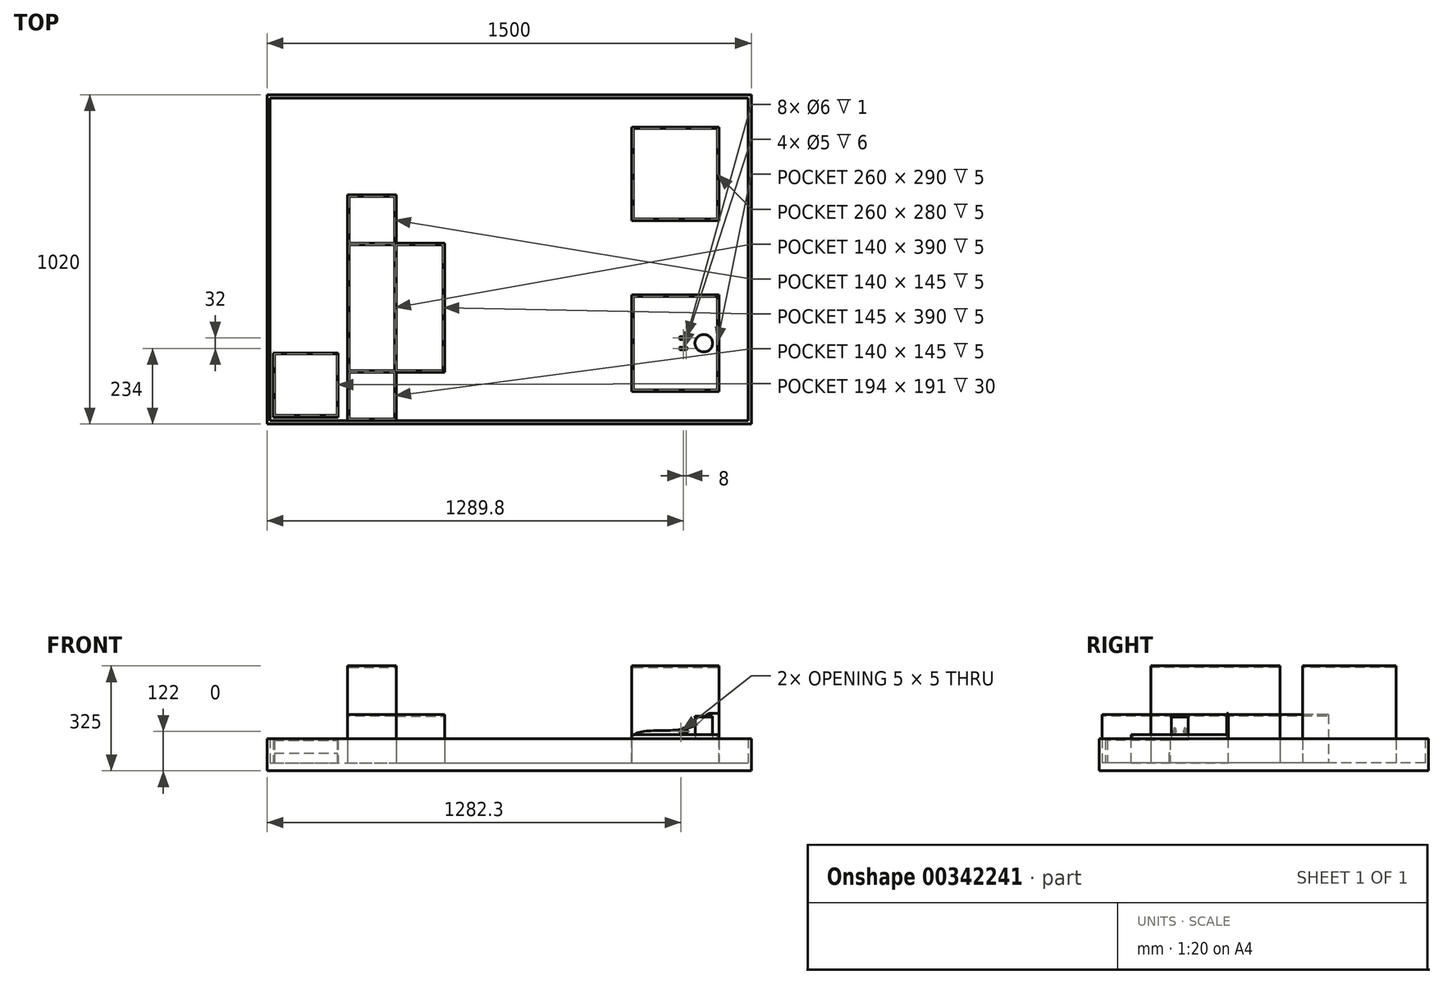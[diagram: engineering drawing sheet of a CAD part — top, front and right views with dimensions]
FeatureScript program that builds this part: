
annotation { "Feature Type Name" : "Feature", "Feature Type Description" : "" }
export const myFeature = defineFeature(function(context is Context, id is Id, definition is map)
    precondition{}
    {
        {
            var Q0;
            Q0=qCreatedBy(makeId("Top.planeOp"),FACE);
            var sketch = newSketch(context, id + "F0", { "sketchPlane" : qUnion([Q0])});
            skCircle(sketch, "E0", {"center": v(0, 0) * mm, "radius": 27.2 * mm});
            skSolve(sketch);
        }
        {
            var Q0;
            Q0=qSketchRegion(id+"F0",true);
            extrude(context, id + "F1", {"entities" : qUnion([Q0]), "depth" : 2.83 * mm});
        }
        {
            var Q0;
            Q0=makeQuery(id+"F1.opExtrude","CAP_FACE",FACE,{"disambiguationData":[OSD([sQuery(id+"F0.wireOp",EDGE,"E0")])],"isStart":false});
            var sketch = newSketch(context, id + "F2", { "sketchPlane" : qUnion([Q0])});
            skCircle(sketch, "E1", {"center": v(0, 0) * mm, "radius": 26.4 * mm});
            skSolve(sketch);
        }
        {
            var Q0;
            Q0=qSketchRegion(id+"F2",true);
            extrude(context, id + "F3", {"entities" : qUnion([Q0]), "operationType" : NewBodyOperationType.ADD, "depth" : 67.36 * mm});
        }
        {
            var Q0;
            Q0=makeQuery(id+"F3.opExtrude","CAP_FACE",FACE,{"disambiguationData":[OSD([sQuery(id+"F2.wireOp",EDGE,"E1")])],"isStart":false});
            var sketch = newSketch(context, id + "F4", { "sketchPlane" : qUnion([Q0])});
            skCircle(sketch, "E2", {"center": v(0, 0) * mm, "radius": 27.2 * mm});
            skSolve(sketch);
        }
        {
            var Q0;
            Q0=qSketchRegion(id+"F4",true);
            extrude(context, id + "F5", {"entities" : qUnion([Q0]), "operationType" : NewBodyOperationType.ADD, "depth" : 2.83 * mm});
        }
        {
            var Q0;
            Q0=makeQuery(id+"F5.opExtrude","CAP_FACE",FACE,{"disambiguationData":[OSD([sQuery(id+"F4.wireOp",EDGE,"E2")])],"isStart":false});
            var sketch = newSketch(context, id + "F6", { "sketchPlane" : qUnion([Q0])});
            skSolve(sketch);
        }
        {
            var Q0;
            Q0=qCreatedBy(makeId("Top.planeOp"),FACE);
            cPlane(context, id + "F7", {"entities" : qUnion([Q0]), "cplaneType" : CPlaneType.OFFSET, "offset" : 25 * mm, "width" : 150 * mm, "height" : 150 * mm});
        }
        {
            var Q0;
            Q0=makeQuery(id+"F6.imprint","IMPRINT",FACE,{"disambiguationData":[TD([[makeQuery(id+"F6.imprint","IMPRINT",EDGE,{"derivedFrom":makeQuery(id+"F5.opExtrude","CAP_EDGE",EDGE,{"disambiguationData":[OSD([sQuery(id+"F4.wireOp",EDGE,"E2")])],"isStart":false})}),1.0]])]});
            var sketch = newSketch(context, id + "F8", { "sketchPlane" : qUnion([Q0])});
            skSolve(sketch);
        }
        {
            var Q0;
            Q0=qCreatedBy(makeId("Top.planeOp"),FACE);
            var sketch = newSketch(context, id + "F9", { "sketchPlane" : qUnion([Q0])});
            skLineSegment(sketch, "E3.bottom", {"start": v(-222.8, -150) * mm, "end": v(47.2, -150) * mm});
            skLineSegment(sketch, "E3.top", {"start": v(-222.8, 150) * mm, "end": v(47.2, 150) * mm});
            skLineSegment(sketch, "E3.left", {"start": v(-222.8, -150) * mm, "end": v(-222.8, 150) * mm});
            skLineSegment(sketch, "E3.right", {"start": v(47.2, -150) * mm, "end": v(47.2, 150) * mm});
            skSolve(sketch);
        }
        {
            var Q0;
            Q0=qSketchRegion(id+"F9",true);
            extrude(context, id + "F10", {"entities" : qUnion([Q0]), "oppositeDirection" : true, "depth" : 72 * mm});
        }
        {
            var Q0;
            Q0=makeQuery(id+"F10.opExtrude","CAP_FACE",FACE,{"disambiguationData":[OSD([sQuery(id+"F9.wireOp",EDGE,"E3.bottom"),sQuery(id+"F9.wireOp",EDGE,"E3.top"),sQuery(id+"F9.wireOp",EDGE,"E3.left"),sQuery(id+"F9.wireOp",EDGE,"E3.right")])],"isStart":true});
            var sketch = newSketch(context, id + "F11", { "sketchPlane" : qUnion([Q0])});
            skLineSegment(sketch, "E4.bottom", {"start": v(-222.8, -150) * mm, "end": v(47.2, -150) * mm});
            skLineSegment(sketch, "E4.top", {"start": v(-222.8, -145) * mm, "end": v(42.2, -145) * mm});
            skLineSegment(sketch, "E4.left", {"start": v(-222.8, -150) * mm, "end": v(-222.8, -145) * mm});
            skLineSegment(sketch, "E5.bottom", {"start": v(47.2, 150) * mm, "end": v(42.2, 150) * mm});
            skLineSegment(sketch, "E5.left", {"start": v(47.2, 150) * mm, "end": v(47.2, -150) * mm});
            skLineSegment(sketch, "E5.right", {"start": v(42.2, 150) * mm, "end": v(42.2, -145) * mm});
            skSolve(sketch);
        }
        {
            var Q0;
            Q0=qSketchRegion(id+"F11",true);
            extrude(context, id + "F12", {"entities" : qUnion([Q0]), "operationType" : NewBodyOperationType.ADD, "depth" : 15 * mm});
        }
        {
            var Q0;
            Q0=makeQuery(id+"F12.boolean.opBoolean","MERGE",FACE,{"derivedFrom":[makeQuery(id+"F10.opExtrude","SWEPT_FACE",FACE,{"disambiguationData":[OSD([sQuery(id+"F9.wireOp",EDGE,"E3.top")])]}),makeQuery(id+"F12.opExtrude","SWEPT_FACE",FACE,{"disambiguationData":[OSD([sQuery(id+"F11.wireOp",EDGE,"E5.bottom")])]})]});
            var sketch = newSketch(context, id + "F13", { "sketchPlane" : qUnion([Q0])});
            skLineSegment(sketch, "E6", {"start": v(-47.2, 81.36) * mm, "end": v(-21.31, 81.36) * mm});
            skFitSpline(sketch, "E7", {"points": [v(-21.31, 81.36) * mm, v(15.24, 52.01) * mm, v(114.14, 28.17) * mm, v(222.8, 0) * mm], "startDerivative": vector(181.02, 0.3) * mm, "endDerivative": vector(-1.73, -239.85) * mm});
            skLineSegment(sketch, "E8", {"start": v(-47.2, 81.36) * mm, "end": v(-47.2, -72) * mm});
            skLineSegment(sketch, "E9", {"start": v(-47.2, -72) * mm, "end": v(222.8, -72) * mm});
            skLineSegment(sketch, "E10", {"start": v(222.8, -72) * mm, "end": v(222.8, 0) * mm});
            skSolve(sketch);
        }
        {
            var Q0;
            Q0=qSketchRegion(id+"F13",true);
            extrude(context, id + "F14", {"entities" : qUnion([Q0]), "operationType" : NewBodyOperationType.ADD, "oppositeDirection" : true, "depth" : 5 * mm});
        }
        {
            var Q0;
            Q0=makeQuery(id+"F10.opExtrude","CAP_FACE",FACE,{"disambiguationData":[OSD([sQuery(id+"F9.wireOp",EDGE,"E3.bottom"),sQuery(id+"F9.wireOp",EDGE,"E3.top"),sQuery(id+"F9.wireOp",EDGE,"E3.left"),sQuery(id+"F9.wireOp",EDGE,"E3.right")])],"isStart":true});
            var sketch = newSketch(context, id + "F15", { "sketchPlane" : qUnion([Q0])});
            skLineSegment(sketch, "E11.bottom", {"start": v(-222.8, 145) * mm, "end": v(-217.8, 145) * mm});
            skLineSegment(sketch, "E11.top", {"start": v(-222.8, -145) * mm, "end": v(-217.8, -145) * mm});
            skLineSegment(sketch, "E11.left", {"start": v(-222.8, 145) * mm, "end": v(-222.8, -145) * mm});
            skLineSegment(sketch, "E11.right", {"start": v(-217.8, 145) * mm, "end": v(-217.8, -145) * mm});
            skSolve(sketch);
        }
        {
            var Q0;
            Q0=qSketchRegion(id+"F15",true);
            extrude(context, id + "F16", {"entities" : qUnion([Q0]), "operationType" : NewBodyOperationType.ADD, "depth" : 5 * mm});
        }
        {
            var Q0;
            Q0=makeQuery(id+"F10.opExtrude","CAP_FACE",FACE,{"disambiguationData":[OSD([sQuery(id+"F9.wireOp",EDGE,"E3.bottom"),sQuery(id+"F9.wireOp",EDGE,"E3.top"),sQuery(id+"F9.wireOp",EDGE,"E3.left"),sQuery(id+"F9.wireOp",EDGE,"E3.right")])],"isStart":false});
            var sketch = newSketch(context, id + "F17", { "sketchPlane" : qUnion([Q0])});
            skLineSegment(sketch, "E12.bottom", {"start": v(147.2, 250) * mm, "end": v(-1352.8, 250) * mm});
            skLineSegment(sketch, "E12.top", {"start": v(147.2, -770) * mm, "end": v(-1352.8, -770) * mm});
            skLineSegment(sketch, "E12.left", {"start": v(147.2, 250) * mm, "end": v(147.2, -770) * mm});
            skLineSegment(sketch, "E12.right", {"start": v(-1352.8, 250) * mm, "end": v(-1352.8, -770) * mm});
            skSolve(sketch);
        }
        {
            var Q0;
            Q0=qSketchRegion(id+"F17",true);
            extrude(context, id + "F18", {"entities" : qUnion([Q0]), "operationType" : NewBodyOperationType.ADD, "depth" : 25 * mm});
        }
        {
            var Q0;
            Q0=makeQuery(id+"F18.opExtrude","CAP_FACE",FACE,{"disambiguationData":[OSD([sQuery(id+"F17.wireOp",EDGE,"E12.bottom"),sQuery(id+"F17.wireOp",EDGE,"E12.top"),sQuery(id+"F17.wireOp",EDGE,"E12.left"),sQuery(id+"F17.wireOp",EDGE,"E12.right")])],"isStart":true});
            var sketch = newSketch(context, id + "F19", { "sketchPlane" : qUnion([Q0])});
            skLineSegment(sketch, "E13.bottom", {"start": v(-222.8, 670) * mm, "end": v(47.2, 670) * mm});
            skLineSegment(sketch, "E13.top", {"start": v(-222.8, 380) * mm, "end": v(47.2, 380) * mm});
            skLineSegment(sketch, "E13.left", {"start": v(-222.8, 670) * mm, "end": v(-222.8, 380) * mm});
            skLineSegment(sketch, "E13.right", {"start": v(47.2, 670) * mm, "end": v(47.2, 380) * mm});
            skSolve(sketch);
        }
        {
            var Q0;
            Q0=qSketchRegion(id+"F19",true);
            extrude(context, id + "F20", {"entities" : qUnion([Q0]), "operationType" : NewBodyOperationType.ADD, "depth" : 300 * mm});
        }
        {
            var Q0;
            Q0=makeQuery(id+"F20.opExtrude","CAP_FACE",FACE,{"disambiguationData":[OSD([sQuery(id+"F19.wireOp",EDGE,"E13.bottom"),sQuery(id+"F19.wireOp",EDGE,"E13.top"),sQuery(id+"F19.wireOp",EDGE,"E13.left"),sQuery(id+"F19.wireOp",EDGE,"E13.right")])],"isStart":false});
            var sketch = newSketch(context, id + "F21", { "sketchPlane" : qUnion([Q0])});
            skLineSegment(sketch, "E14.bottom", {"start": v(-217.8, 665) * mm, "end": v(42.2, 665) * mm});
            skLineSegment(sketch, "E14.top", {"start": v(-217.8, 385) * mm, "end": v(42.2, 385) * mm});
            skLineSegment(sketch, "E14.left", {"start": v(-217.8, 665) * mm, "end": v(-217.8, 385) * mm});
            skLineSegment(sketch, "E14.right", {"start": v(42.2, 665) * mm, "end": v(42.2, 385) * mm});
            skSolve(sketch);
        }
        {
            var Q0;
            Q0=qSketchRegion(id+"F21",true);
            extrude(context, id + "F22", {"entities" : qUnion([Q0]), "operationType" : NewBodyOperationType.REMOVE, "oppositeDirection" : true, "depth" : 5 * mm});
        }
        {
            var Q0;
            Q0=makeQuery(id+"F18.opExtrude","CAP_FACE",FACE,{"disambiguationData":[OSD([sQuery(id+"F17.wireOp",EDGE,"E12.bottom"),sQuery(id+"F17.wireOp",EDGE,"E12.top"),sQuery(id+"F17.wireOp",EDGE,"E12.left"),sQuery(id+"F17.wireOp",EDGE,"E12.right")])],"isStart":true});
            var sketch = newSketch(context, id + "F23", { "sketchPlane" : qUnion([Q0])});
            skLineSegment(sketch, "E15.bottom", {"start": v(-1352.8, 770) * mm, "end": v(147.2, 770) * mm});
            skLineSegment(sketch, "E15.top", {"start": v(-1352.8, -250) * mm, "end": v(147.2, -250) * mm});
            skLineSegment(sketch, "E15.left", {"start": v(-1352.8, 770) * mm, "end": v(-1352.8, -250) * mm});
            skLineSegment(sketch, "E15.right", {"start": v(147.2, 770) * mm, "end": v(147.2, -250) * mm});
            skLineSegment(sketch, "E16.bottom", {"start": v(-1342.8, 760) * mm, "end": v(137.2, 760) * mm});
            skLineSegment(sketch, "E16.top", {"start": v(-1342.8, -240) * mm, "end": v(137.2, -240) * mm});
            skLineSegment(sketch, "E16.left", {"start": v(-1342.8, 760) * mm, "end": v(-1342.8, -240) * mm});
            skLineSegment(sketch, "E16.right", {"start": v(137.2, 760) * mm, "end": v(137.2, -240) * mm});
            skSolve(sketch);
        }
        {
            var Q0;
            Q0=qSketchRegion(id+"F23",true);
            extrude(context, id + "F24", {"entities" : qUnion([Q0]), "operationType" : NewBodyOperationType.ADD, "depth" : 75 * mm});
        }
        {
            var Q0;
            Q0=makeQuery(id+"F18.opExtrude","CAP_FACE",FACE,{"disambiguationData":[OSD([sQuery(id+"F17.wireOp",EDGE,"E12.bottom"),sQuery(id+"F17.wireOp",EDGE,"E12.top"),sQuery(id+"F17.wireOp",EDGE,"E12.left"),sQuery(id+"F17.wireOp",EDGE,"E12.right")])],"isStart":true});
            var sketch = newSketch(context, id + "F25", { "sketchPlane" : qUnion([Q0])});
            skLineSegment(sketch, "E17.bottom", {"start": v(-1102.8, 460) * mm, "end": v(-952.8, 460) * mm});
            skLineSegment(sketch, "E17.top", {"start": v(-1102.8, -240) * mm, "end": v(-952.8, -240) * mm});
            skLineSegment(sketch, "E17.left", {"start": v(-1102.8, 460) * mm, "end": v(-1102.8, -240) * mm});
            skLineSegment(sketch, "E17.right", {"start": v(-952.8, 460) * mm, "end": v(-952.8, 310) * mm});
            skLineSegment(sketch, "E18.bottom", {"start": v(-952.8, 310) * mm, "end": v(-802.8, 310) * mm});
            skLineSegment(sketch, "E18.top", {"start": v(-952.8, -90) * mm, "end": v(-802.8, -90) * mm});
            skLineSegment(sketch, "E18.right", {"start": v(-802.8, 310) * mm, "end": v(-802.8, -90) * mm});
            skLineSegment(sketch, "E19.trimOffspring", {"start": v(-952.8, -90) * mm, "end": v(-952.8, -240) * mm});
            skSolve(sketch);
        }
        {
            var Q0;
            Q0=qSketchRegion(id+"F25",true);
            extrude(context, id + "F26", {"entities" : qUnion([Q0]), "operationType" : NewBodyOperationType.ADD, "depth" : 150 * mm});
        }
        {
            var Q0;
            Q0=makeQuery(id+"F26.opExtrude","CAP_FACE",FACE,{"disambiguationData":[OSD([sQuery(id+"F25.wireOp",EDGE,"E17.bottom"),sQuery(id+"F25.wireOp",EDGE,"E17.top"),sQuery(id+"F25.wireOp",EDGE,"E17.left"),sQuery(id+"F25.wireOp",EDGE,"E17.right"),sQuery(id+"F25.wireOp",EDGE,"E18.bottom"),sQuery(id+"F25.wireOp",EDGE,"E18.top"),sQuery(id+"F25.wireOp",EDGE,"E18.right"),sQuery(id+"F25.wireOp",EDGE,"E19.trimOffspring")])],"isStart":false});
            var sketch = newSketch(context, id + "F27", { "sketchPlane" : qUnion([Q0])});
            skLineSegment(sketch, "E20.bottom", {"start": v(-952.8, 310) * mm, "end": v(-1102.8, 310) * mm});
            skLineSegment(sketch, "E20.top", {"start": v(-952.8, -90) * mm, "end": v(-1102.8, -90) * mm});
            skLineSegment(sketch, "E20.left", {"start": v(-952.8, 310) * mm, "end": v(-952.8, -90) * mm});
            skLineSegment(sketch, "E20.right", {"start": v(-1102.8, 310) * mm, "end": v(-1102.8, -90) * mm});
            skSolve(sketch);
        }
        {
            var Q0;
            Q0=qSketchRegion(id+"F27",true);
            extrude(context, id + "F28", {"entities" : qUnion([Q0]), "operationType" : NewBodyOperationType.ADD, "depth" : 150 * mm});
        }
        {
            var Q0;
            Q0=makeQuery(id+"F28.opExtrude","CAP_FACE",FACE,{"disambiguationData":[OSD([sQuery(id+"F27.wireOp",EDGE,"E20.bottom"),sQuery(id+"F27.wireOp",EDGE,"E20.top"),sQuery(id+"F27.wireOp",EDGE,"E20.left"),sQuery(id+"F27.wireOp",EDGE,"E20.right")])],"isStart":false});
            var sketch = newSketch(context, id + "F29", { "sketchPlane" : qUnion([Q0])});
            skLineSegment(sketch, "E21.bottom", {"start": v(-1097.8, 305) * mm, "end": v(-957.8, 305) * mm});
            skLineSegment(sketch, "E21.top", {"start": v(-1097.8, -85) * mm, "end": v(-957.8, -85) * mm});
            skLineSegment(sketch, "E21.left", {"start": v(-1097.8, 305) * mm, "end": v(-1097.8, -85) * mm});
            skLineSegment(sketch, "E21.right", {"start": v(-957.8, 305) * mm, "end": v(-957.8, -85) * mm});
            skSolve(sketch);
        }
        {
            var Q0;
            Q0=qSketchRegion(id+"F29",true);
            extrude(context, id + "F30", {"entities" : qUnion([Q0]), "operationType" : NewBodyOperationType.REMOVE, "oppositeDirection" : true, "depth" : 5 * mm});
        }
        {
            var Q0;
            {var subQ0=sQuery(id+"F25.wireOp",EDGE,"E17.left");var subQ1=sQuery(id+"F25.wireOp",EDGE,"E18.bottom");var subQ2=sQuery(id+"F25.wireOp",EDGE,"E17.right");var subQ3=sQuery(id+"F25.wireOp",EDGE,"E17.bottom");var subQ4=makeQuery(id+"F26.opExtrude","CAP_FACE",FACE,{"disambiguationData":[OSD([subQ3,sQuery(id+"F25.wireOp",EDGE,"E17.top"),subQ0,subQ2,subQ1,sQuery(id+"F25.wireOp",EDGE,"E18.top"),sQuery(id+"F25.wireOp",EDGE,"E18.right"),sQuery(id+"F25.wireOp",EDGE,"E19.trimOffspring")])],"isStart":false});Q0=makeQuery(id+"F28.boolean.opBoolean","SPLIT",FACE,{"disambiguationData":[TD([makeQuery(id+"F26.opExtrude","SWEPT_FACE",FACE,{"disambiguationData":[OSD([subQ3])]})])],"derivedFrom":subQ4});}
            var sketch = newSketch(context, id + "F31", { "sketchPlane" : qUnion([Q0])});
            skLineSegment(sketch, "E22.bottom", {"start": v(-1097.8, 455) * mm, "end": v(-957.8, 455) * mm});
            skLineSegment(sketch, "E22.top", {"start": v(-1097.8, 310) * mm, "end": v(-957.8, 310) * mm});
            skLineSegment(sketch, "E22.left", {"start": v(-1097.8, 455) * mm, "end": v(-1097.8, 310) * mm});
            skLineSegment(sketch, "E22.right", {"start": v(-957.8, 455) * mm, "end": v(-957.8, 310) * mm});
            skLineSegment(sketch, "E23.bottom", {"start": v(-952.8, 305) * mm, "end": v(-807.8, 305) * mm});
            skLineSegment(sketch, "E23.top", {"start": v(-952.8, -85) * mm, "end": v(-807.8, -85) * mm});
            skLineSegment(sketch, "E23.left", {"start": v(-952.8, 305) * mm, "end": v(-952.8, -85) * mm});
            skLineSegment(sketch, "E23.right", {"start": v(-807.8, 305) * mm, "end": v(-807.8, -85) * mm});
            skLineSegment(sketch, "E24.bottom", {"start": v(-1097.8, -90) * mm, "end": v(-957.8, -90) * mm});
            skLineSegment(sketch, "E24.top", {"start": v(-1097.8, -235) * mm, "end": v(-957.8, -235) * mm});
            skLineSegment(sketch, "E24.left", {"start": v(-1097.8, -90) * mm, "end": v(-1097.8, -235) * mm});
            skLineSegment(sketch, "E24.right", {"start": v(-957.8, -90) * mm, "end": v(-957.8, -235) * mm});
            skSolve(sketch);
        }
        {
            var Q0;
            Q0=qSketchRegion(id+"F31",true);
            extrude(context, id + "F32", {"entities" : qUnion([Q0]), "operationType" : NewBodyOperationType.REMOVE, "oppositeDirection" : true, "depth" : 5 * mm});
        }
        {
            var Q0;
            Q0=qCreatedBy(id+"F7.planeOp",FACE);
            var sketch = newSketch(context, id + "F33", { "sketchPlane" : qUnion([Q0])});
            skLineSegment(sketch, "E25", {"start": v(0, 0) * mm, "end": v(-90, 0) * mm, "construction": true});
            skLineSegment(sketch, "E26.bottom", {"start": v(-74.5, -12) * mm, "end": v(-55, -12) * mm});
            skLineSegment(sketch, "E26.top", {"start": v(-74.5, -20) * mm, "end": v(-55, -20) * mm});
            skLineSegment(sketch, "E26.left", {"start": v(-74.5, -12) * mm, "end": v(-74.5, -13) * mm});
            skPoint(sketch, "E27.visualSharp", {"position": v(-51, -12) * mm});
            skPoint(sketch, "E28.visualSharp", {"position": v(-51, -20) * mm});
            skCircle(sketch, "E29", {"center": v(-55, -16) * mm, "radius": 3 * mm});
            skLineSegment(sketch, "E30", {"start": v(-59, -3.98) * mm, "end": v(-59, -18.08) * mm, "construction": true});
            skCircle(sketch, "E31.MirrorC", {"center": v(-63, -16) * mm, "radius": 3 * mm});
            skLineSegment(sketch, "E32.bottom", {"start": v(-74.5, -13) * mm, "end": v(-65.65, -13) * mm});
            skLineSegment(sketch, "E32.top", {"start": v(-74.5, -19) * mm, "end": v(-65.65, -19) * mm});
            skArc(sketch, "E33", {"start": v(-65.65, -13) * mm, "mid": v(-67, -16) * mm, "end": v(-65.65, -19) * mm});
            skLineSegment(sketch, "E34.trimOffspring", {"start": v(-74.5, -19) * mm, "end": v(-74.5, -20) * mm});
            skArc(sketch, "E35.trimOffspring", {"start": v(-55, -20) * mm, "mid": v(-51, -16) * mm, "end": v(-55, -12) * mm});
            skLineSegment(sketch, "E36.MirrorCS", {"start": v(-74.5, 12) * mm, "end": v(-74.5, 13) * mm});
            skLineSegment(sketch, "E37.MirrorCS", {"start": v(-74.5, 19) * mm, "end": v(-74.5, 20) * mm});
            skPoint(sketch, "E38.MirrorP", {"position": v(-51, 12) * mm});
            skLineSegment(sketch, "E39.MirrorCS", {"start": v(-74.5, 12) * mm, "end": v(-55, 12) * mm});
            skPoint(sketch, "E40.MirrorP", {"position": v(-51, 20) * mm});
            skArc(sketch, "E41.MirrorCS", {"start": v(-65.65, 13) * mm, "mid": v(-67, 16) * mm, "end": v(-65.65, 19) * mm});
            skArc(sketch, "E42.MirrorCS", {"start": v(-55, 20) * mm, "mid": v(-51, 16) * mm, "end": v(-55, 12) * mm});
            skLineSegment(sketch, "E43.MirrorCS", {"start": v(-74.5, 20) * mm, "end": v(-55, 20) * mm});
            skCircle(sketch, "E44.MirrorC", {"center": v(-55, 16) * mm, "radius": 3 * mm});
            skCircle(sketch, "E45.MirrorC", {"center": v(-63, 16) * mm, "radius": 3 * mm});
            skLineSegment(sketch, "E46.MirrorCS", {"start": v(-74.5, 19) * mm, "end": v(-65.65, 19) * mm});
            skLineSegment(sketch, "E47.MirrorCS", {"start": v(-74.5, 13) * mm, "end": v(-65.65, 13) * mm});
            skSolve(sketch);
        }
        {
            var Q0;
            Q0=qSketchRegion(id+"F33",true);
            var Q1;
            Q1=qSketchRegion(id+"F36",true);
            extrude(context, id + "F34", {"entities" : qUnion([Q0, Q1]), "endBound" : BoundingType.SYMMETRIC, "depth" : 8 * mm});
        }
        {
            var Q0;
            Q0=makeQuery(id+"F34.opExtrude","CAP_EDGE",EDGE,{"disambiguationData":[OSD([sQuery(id+"F33.wireOp",EDGE,"E34.trimOffspring")])],"isStart":false});
            var Q1;
            Q1=makeQuery(id+"F34.opExtrude","CAP_EDGE",EDGE,{"disambiguationData":[OSD([sQuery(id+"F33.wireOp",EDGE,"E26.left")])],"isStart":false});
            var Q2;
            Q2=makeQuery(id+"F34.opExtrude","CAP_EDGE",EDGE,{"disambiguationData":[OSD([sQuery(id+"F33.wireOp",EDGE,"E34.trimOffspring")])],"isStart":true});
            var Q3;
            Q3=makeQuery(id+"F34.opExtrude","CAP_EDGE",EDGE,{"disambiguationData":[OSD([sQuery(id+"F33.wireOp",EDGE,"E26.left")])],"isStart":true});
            var Q4;
            Q4=makeQuery(id+"F34.opExtrude","CAP_EDGE",EDGE,{"disambiguationData":[OSD([sQuery(id+"F33.wireOp",EDGE,"E36.MirrorCS")])],"isStart":false});
            var Q5;
            Q5=makeQuery(id+"F34.opExtrude","CAP_EDGE",EDGE,{"disambiguationData":[OSD([sQuery(id+"F33.wireOp",EDGE,"E37.MirrorCS")])],"isStart":false});
            var Q6;
            Q6=makeQuery(id+"F34.opExtrude","CAP_EDGE",EDGE,{"disambiguationData":[OSD([sQuery(id+"F33.wireOp",EDGE,"E37.MirrorCS")])],"isStart":true});
            var Q7;
            Q7=makeQuery(id+"F34.opExtrude","CAP_EDGE",EDGE,{"disambiguationData":[OSD([sQuery(id+"F33.wireOp",EDGE,"E36.MirrorCS")])],"isStart":true});
            fillet(context, id + "F35", {"entities" : qUnion([Q0, Q1, Q2, Q3, Q4, Q5, Q6, Q7]), "radius" : 4 * mm, "tangentPropagation" : true, "allowEdgeOverflow" : false});
        }
        {
            var Q0;
            Q0=makeQuery(id+"F34.opExtrude","SWEPT_FACE",FACE,{"disambiguationData":[OSD([sQuery(id+"F33.wireOp",EDGE,"E26.top")])]});
            var sketch = newSketch(context, id + "F36", { "sketchPlane" : qUnion([Q0])});
            skCircle(sketch, "E48", {"center": v(-70.5, 25) * mm, "radius": 3 * mm});
            skSolve(sketch);
        }
        {
            var Q0;
            Q0=qSketchRegion(id+"F36",true);
            var Q1;
            Q1=makeQuery(id+"F34.opExtrude","SWEPT_FACE",FACE,{"disambiguationData":[OSD([sQuery(id+"F33.wireOp",EDGE,"E26.bottom")])]});
            extrude(context, id + "F37", {"entities" : qUnion([Q0]), "operationType" : NewBodyOperationType.ADD, "endBound" : BoundingType.UP_TO_SURFACE, "oppositeDirection" : true, "endBoundEntityFace" : qUnion([Q1]), "depth" : 25 * mm});
        }
        {
            var Q0;
            Q0=makeQuery(id+"F34.opExtrude","SWEPT_FACE",FACE,{"disambiguationData":[OSD([sQuery(id+"F33.wireOp",EDGE,"E43.MirrorCS")])]});
            var sketch = newSketch(context, id + "F38", { "sketchPlane" : qUnion([Q0])});
            skCircle(sketch, "E49", {"center": v(70.5, 25) * mm, "radius": 3 * mm});
            skSolve(sketch);
        }
        {
            var Q0;
            Q0=qSketchRegion(id+"F38",true);
            var Q1;
            Q1=makeQuery(id+"F34.opExtrude","SWEPT_FACE",FACE,{"disambiguationData":[OSD([sQuery(id+"F33.wireOp",EDGE,"E39.MirrorCS")])]});
            extrude(context, id + "F39", {"entities" : qUnion([Q0]), "operationType" : NewBodyOperationType.ADD, "endBound" : BoundingType.UP_TO_SURFACE, "oppositeDirection" : true, "endBoundEntityFace" : qUnion([Q1]), "depth" : 25 * mm});
        }
        {
            var Q0;
            Q0=qCreatedBy(id+"F7.planeOp",FACE);
            var sketch = newSketch(context, id + "F40", { "sketchPlane" : qUnion([Q0])});
            skCircle(sketch, "E50", {"center": v(-55, 16) * mm, "radius": 3 * mm});
            skCircle(sketch, "E51", {"center": v(-63, 16) * mm, "radius": 2.5 * mm});
            skCircle(sketch, "E52", {"center": v(-63, 16) * mm, "radius": 3 * mm});
            skCircle(sketch, "E53", {"center": v(-55, 16) * mm, "radius": 2.5 * mm});
            skSolve(sketch);
        }
        {
            var Q0;
            Q0=qSketchRegion(id+"F40",true);
            extrude(context, id + "F41", {"entities" : qUnion([Q0]), "operationType" : NewBodyOperationType.ADD, "endBound" : BoundingType.SYMMETRIC, "depth" : 6 * mm});
        }
        {
            var Q0;
            Q0=qCreatedBy(id+"F7.planeOp",FACE);
            var sketch = newSketch(context, id + "F42", { "sketchPlane" : qUnion([Q0])});
            skCircle(sketch, "E54", {"center": v(-63, -16) * mm, "radius": 2.5 * mm});
            skCircle(sketch, "E55", {"center": v(-63, -16) * mm, "radius": 3 * mm});
            skCircle(sketch, "E56", {"center": v(-55, -16) * mm, "radius": 2.5 * mm});
            skCircle(sketch, "E57", {"center": v(-55, -16) * mm, "radius": 3 * mm});
            skSolve(sketch);
        }
        {
            var Q0;
            Q0=qSketchRegion(id+"F42",true);
            extrude(context, id + "F43", {"entities" : qUnion([Q0]), "operationType" : NewBodyOperationType.ADD, "endBound" : BoundingType.SYMMETRIC, "depth" : 6 * mm});
        }
        {
            var Q0;
            Q0=makeQuery(id+"F34.opExtrude","SWEPT_FACE",FACE,{"disambiguationData":[OSD([sQuery(id+"F33.wireOp",EDGE,"E43.MirrorCS")])]});
            var sketch = newSketch(context, id + "F44", { "sketchPlane" : qUnion([Q0])});
            skArc(sketch, "E58", {"start": v(71.5, 27.3) * mm, "mid": v(70.5, 27.5) * mm, "end": v(69.5, 27.3) * mm});
            skLineSegment(sketch, "E59.bottom", {"start": v(68.2, 26) * mm, "end": v(69.5, 26) * mm});
            skLineSegment(sketch, "E59.top", {"start": v(68.2, 24) * mm, "end": v(69.5, 24) * mm});
            skLineSegment(sketch, "E60.left", {"start": v(71.5, 27.3) * mm, "end": v(71.5, 26) * mm});
            skLineSegment(sketch, "E60.right", {"start": v(69.5, 27.3) * mm, "end": v(69.5, 26) * mm});
            skPoint(sketch, "E61.orphan", {"position": v(69.5, 27.8) * mm});
            skPoint(sketch, "E62.orphan", {"position": v(71.5, 27.8) * mm});
            skArc(sketch, "E63.trimOffspring", {"start": v(68.2, 26) * mm, "mid": v(68, 25) * mm, "end": v(68.2, 24) * mm});
            skPoint(sketch, "E59.left.start.orphan", {"position": v(67.32, 26) * mm});
            skPoint(sketch, "E64.orphan", {"position": v(67.32, 24) * mm});
            skArc(sketch, "E65.trimOffspring", {"start": v(69.5, 22.7) * mm, "mid": v(70.5, 22.5) * mm, "end": v(71.5, 22.7) * mm});
            skLineSegment(sketch, "E66.trimOffspring", {"start": v(69.5, 24) * mm, "end": v(69.5, 22.7) * mm});
            skLineSegment(sketch, "E67.trimOffspring", {"start": v(71.5, 26) * mm, "end": v(72.8, 26) * mm});
            skLineSegment(sketch, "E68.trimOffspring", {"start": v(71.5, 24) * mm, "end": v(71.5, 22.7) * mm});
            skLineSegment(sketch, "E69.trimOffspring", {"start": v(71.5, 24) * mm, "end": v(72.8, 24) * mm});
            skPoint(sketch, "E60.top.end.orphan", {"position": v(69.5, 22.2) * mm});
            skPoint(sketch, "E70.orphan", {"position": v(71.5, 22.2) * mm});
            skPoint(sketch, "E59.right.end.orphan", {"position": v(73.68, 24) * mm});
            skPoint(sketch, "E71.orphan", {"position": v(73.68, 26) * mm});
            skArc(sketch, "E72.trimOffspring", {"start": v(72.8, 24) * mm, "mid": v(73, 25) * mm, "end": v(72.8, 26) * mm});
            skSolve(sketch);
        }
        {
            var Q0;
            Q0=qSketchRegion(id+"F44",true);
            extrude(context, id + "F45", {"entities" : qUnion([Q0]), "operationType" : NewBodyOperationType.REMOVE, "endBound" : BoundingType.THROUGH_ALL, "oppositeDirection" : true, "depth" : 25 * mm});
        }
        {
            var Q0;
            Q0=makeQuery(id+"F18.opExtrude","CAP_FACE",FACE,{"disambiguationData":[OSD([sQuery(id+"F17.wireOp",EDGE,"E12.bottom"),sQuery(id+"F17.wireOp",EDGE,"E12.top"),sQuery(id+"F17.wireOp",EDGE,"E12.left"),sQuery(id+"F17.wireOp",EDGE,"E12.right")])],"isStart":true});
            var sketch = newSketch(context, id + "F46", { "sketchPlane" : qUnion([Q0])});
            skLineSegment(sketch, "E73.bottom", {"start": v(-1332.8, -30) * mm, "end": v(-1132.8, -30) * mm});
            skLineSegment(sketch, "E73.top", {"start": v(-1332.8, -230) * mm, "end": v(-1132.8, -230) * mm});
            skLineSegment(sketch, "E73.left", {"start": v(-1332.8, -30) * mm, "end": v(-1332.8, -230) * mm});
            skLineSegment(sketch, "E73.right", {"start": v(-1132.8, -30) * mm, "end": v(-1132.8, -230) * mm});
            skLineSegment(sketch, "E74.bottom", {"start": v(-1329.8, -33) * mm, "end": v(-1135.8, -33) * mm});
            skLineSegment(sketch, "E74.top", {"start": v(-1329.8, -224) * mm, "end": v(-1135.8, -224) * mm});
            skLineSegment(sketch, "E74.left", {"start": v(-1329.8, -33) * mm, "end": v(-1329.8, -224) * mm});
            skLineSegment(sketch, "E74.right", {"start": v(-1135.8, -33) * mm, "end": v(-1135.8, -224) * mm});
            skSolve(sketch);
        }
        {
            var Q0;
            Q0=qSketchRegion(id+"F46",true);
            extrude(context, id + "F47", {"entities" : qUnion([Q0]), "operationType" : NewBodyOperationType.ADD, "depth" : 30 * mm});
        }
        {
            var Q0;
            Q0=makeQuery(id+"F47.opExtrude","CAP_FACE",FACE,{"disambiguationData":[OSD([sQuery(id+"F46.wireOp",EDGE,"E73.bottom"),sQuery(id+"F46.wireOp",EDGE,"E73.top"),sQuery(id+"F46.wireOp",EDGE,"E73.left"),sQuery(id+"F46.wireOp",EDGE,"E73.right"),sQuery(id+"F46.wireOp",EDGE,"E74.bottom"),sQuery(id+"F46.wireOp",EDGE,"E74.top"),sQuery(id+"F46.wireOp",EDGE,"E74.left"),sQuery(id+"F46.wireOp",EDGE,"E74.right")])],"isStart":false});
            var sketch = newSketch(context, id + "F48", { "sketchPlane" : qUnion([Q0])});
            skLineSegment(sketch, "E75.bottom", {"start": v(-1332.8, -30) * mm, "end": v(-1329.8, -30) * mm});
            skLineSegment(sketch, "E75.top", {"start": v(-1332.8, -230) * mm, "end": v(-1329.8, -230) * mm});
            skLineSegment(sketch, "E75.left", {"start": v(-1332.8, -30) * mm, "end": v(-1332.8, -230) * mm});
            skLineSegment(sketch, "E75.right", {"start": v(-1329.8, -30) * mm, "end": v(-1329.8, -224) * mm});
            skLineSegment(sketch, "E76.bottom", {"start": v(-1329.8, -230) * mm, "end": v(-1135.8, -230) * mm});
            skLineSegment(sketch, "E76.top", {"start": v(-1329.8, -224) * mm, "end": v(-1135.8, -224) * mm});
            skLineSegment(sketch, "E77.bottom", {"start": v(-1135.8, -230) * mm, "end": v(-1132.8, -230) * mm});
            skLineSegment(sketch, "E77.top", {"start": v(-1135.8, -30) * mm, "end": v(-1132.8, -30) * mm});
            skLineSegment(sketch, "E77.left", {"start": v(-1135.8, -224) * mm, "end": v(-1135.8, -30) * mm});
            skLineSegment(sketch, "E77.right", {"start": v(-1132.8, -230) * mm, "end": v(-1132.8, -30) * mm});
            skSolve(sketch);
        }
        {
            var Q0;
            Q0=qSketchRegion(id+"F48",true);
            extrude(context, id + "F49", {"entities" : qUnion([Q0]), "operationType" : NewBodyOperationType.ADD, "depth" : 40 * mm});
        }
        {
            var Q0;
            Q0=makeQuery(id+"F34.opExtrude","CAP_FACE",FACE,{"disambiguationData":[OSD([sQuery(id+"F33.wireOp",EDGE,"E36.MirrorCS"),sQuery(id+"F33.wireOp",EDGE,"E37.MirrorCS"),sQuery(id+"F33.wireOp",EDGE,"E39.MirrorCS"),sQuery(id+"F33.wireOp",EDGE,"E41.MirrorCS"),sQuery(id+"F33.wireOp",EDGE,"E42.MirrorCS"),sQuery(id+"F33.wireOp",EDGE,"E43.MirrorCS"),sQuery(id+"F33.wireOp",EDGE,"E44.MirrorC"),sQuery(id+"F33.wireOp",EDGE,"E45.MirrorC"),sQuery(id+"F33.wireOp",EDGE,"E46.MirrorCS"),sQuery(id+"F33.wireOp",EDGE,"E47.MirrorCS")])],"isStart":false});
            var sketch = newSketch(context, id + "F50", { "sketchPlane" : qUnion([Q0])});
            skLineSegment(sketch, "E78", {"start": v(-74.3, -20.27) * mm, "end": v(-37.61, -20.27) * mm});
            skLineSegment(sketch, "E79", {"start": v(-74.54, -11.95) * mm, "end": v(-37.61, -7.24) * mm});
            skArc(sketch, "E80", {"start": v(-37.61, -20.27) * mm, "mid": v(-10.47, -45.9) * mm, "end": v(23.27, -29.9) * mm});
            skPoint(sketch, "E81", {"position": v(-74.08, 19.82) * mm});
            skPoint(sketch, "E82", {"position": v(-74.08, 11.5) * mm});
            skLineSegment(sketch, "E83", {"start": v(-74.54, -20.27) * mm, "end": v(-74.54, -11.95) * mm});
            skLineSegment(sketch, "E84", {"start": v(-74.08, 19.82) * mm, "end": v(-74.08, 11.5) * mm});
            skLineSegment(sketch, "E85", {"start": v(-74.08, 19.82) * mm, "end": v(-37.61, 19.98) * mm});
            skLineSegment(sketch, "E86", {"start": v(-74.08, 11.5) * mm, "end": v(-37.61, 5.82) * mm});
            skArc(sketch, "E87", {"start": v(-37.61, -7.24) * mm, "mid": v(-33.13, -0.7) * mm, "end": v(-37.61, 5.82) * mm});
            skArc(sketch, "E88", {"start": v(23.27, 30.24) * mm, "mid": v(-10.75, 46.4) * mm, "end": v(-37.61, 19.98) * mm});
            skLineSegment(sketch, "E89", {"start": v(23.27, 30.24) * mm, "end": v(23.27, 26.24) * mm});
            skLineSegment(sketch, "E90", {"start": v(23.27, -29.9) * mm, "end": v(23.27, -25.9) * mm});
            skArc(sketch, "E91", {"start": v(23.27, 26.24) * mm, "mid": v(-28.05, 0.17) * mm, "end": v(23.27, -25.9) * mm});
            skCircle(sketch, "E92", {"center": v(-63, 16) * mm, "radius": 2.54 * mm});
            skCircle(sketch, "E93", {"center": v(-55, 16) * mm, "radius": 2.63 * mm});
            skCircle(sketch, "E94", {"center": v(-55, -16) * mm, "radius": 2.46 * mm});
            skCircle(sketch, "E95", {"center": v(-63, -16) * mm, "radius": 2.46 * mm});
            skSolve(sketch);
        }
        {
            var Q0;
            Q0 = qSketchRegion(id + "F50", true);
            extrude(context, id + "F51", {"entities" : qUnion([Q0]), "depth" : 6 * mm});
        }
    });
